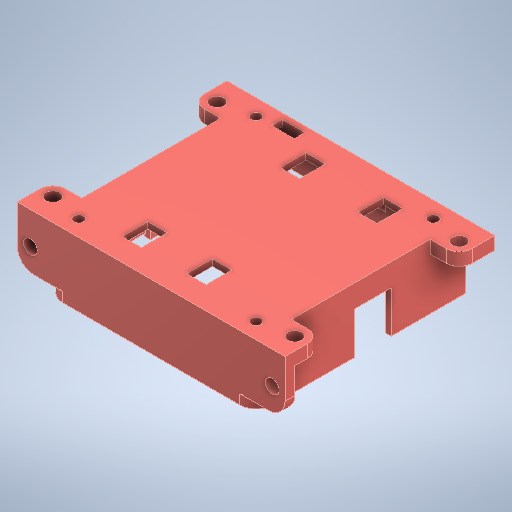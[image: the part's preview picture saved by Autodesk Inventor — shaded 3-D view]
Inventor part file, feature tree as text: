
AUTODESK INVENTOR PART (.ipt)
format: ipt  version: 2025.2 (Build 292293000, 293)  size: 423,936 bytes
history: native  units: in
note: dims shown in document units (in); Inventor stores cm internally (conversion verified against a paired STEP export)
features: extrude x3, sketch x3, other x3, fillet x2, direct_edit x1, projected_geometry x1
ambient origin geometry x8: Origin, YZ Plane, XZ Plane, XY Plane, X Axis, Y Axis, Z Axis, Center Point
bodies: Solid1 (feature_tree)
feature tree (13):
  direct_edit  "Direct Edit1"
  extrude  "Extrusion1"  Depth=0.4331in
  fillet  "Fillet1"  Radius=0.3543in
  fillet  "Fillet2"  Radius=0.4331in
  extrude  "Extrusion2"  Depth=0.1575in
  extrude  "Extrusion3"  Depth=0.1575in
  sketch  "Sketch1"  dims[d0=0.3543in d1=0.4331in d2=0.3543in d3=0.4331in]
  sketch  "Sketch2"  dims[d4=0.1575in d5=0.0in d6=0.1575in]
  sketch  "Sketch3"  dims[d7=0.1575in d8=1.0885in d9=0.1667in d10=0.1667in d11=1.0866in d12=0.1575in d13=0.0in d14=0.1667in d15=0.1575in d16=0.0in]
  projected_geometry  "Projected Loop1"
  other  "Com_Top_A"
  other  "Delete1"
  other  "Delete2"
